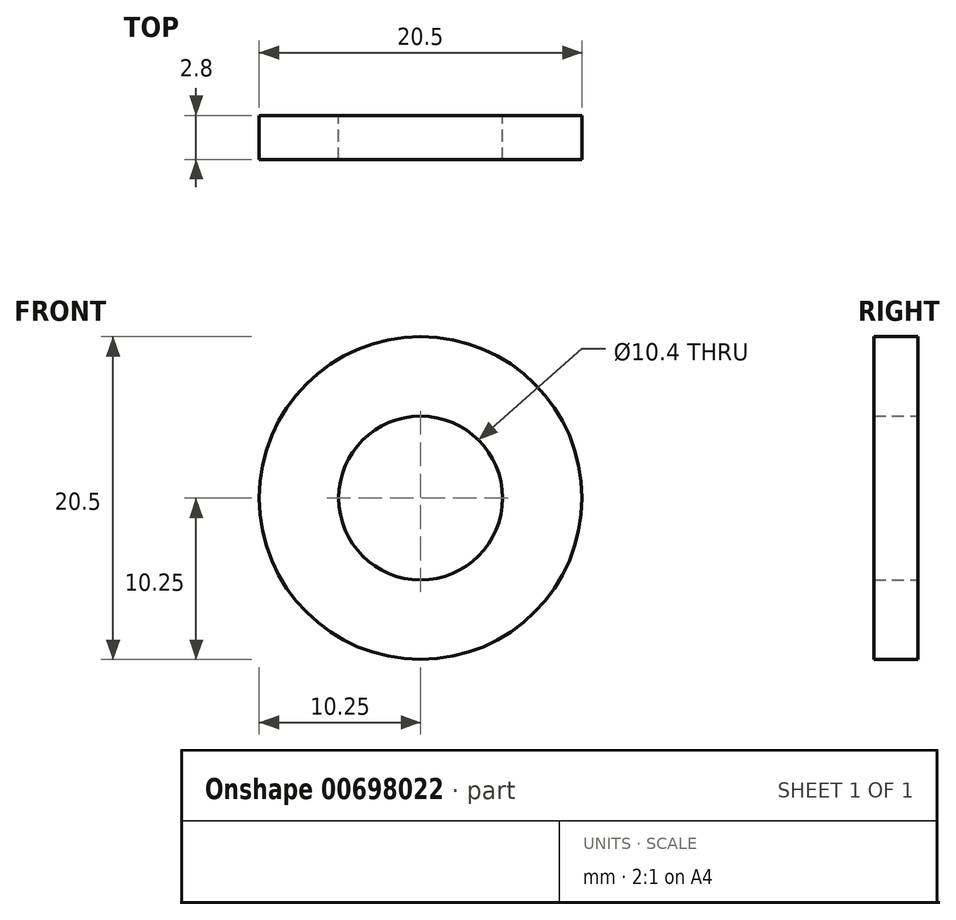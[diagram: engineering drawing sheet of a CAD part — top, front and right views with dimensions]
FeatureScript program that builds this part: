
annotation { "Feature Type Name" : "Feature", "Feature Type Description" : "" }
export const myFeature = defineFeature(function(context is Context, id is Id, definition is map)
    precondition{}
    {
        {
            var Q0;
            Q0=qCreatedBy(makeId("Front.planeOp"),FACE);
            var sketch = newSketch(context, id + "F0", { "sketchPlane" : qUnion([Q0])});
            skCircle(sketch, "E0", {"center": v(0, 0) * mm, "radius": 10.25 * mm});
            skCircle(sketch, "E1", {"center": v(0, 0) * mm, "radius": 5.2 * mm});
            skSolve(sketch);
        }
        {
            var Q0;
            Q0=qSketchRegion(id+"F0",true);
            extrude(context, id + "F1", {"entities" : qUnion([Q0]), "depth" : 2.8 * mm, "offsetDistance" : 25 * mm});
        }
    });
